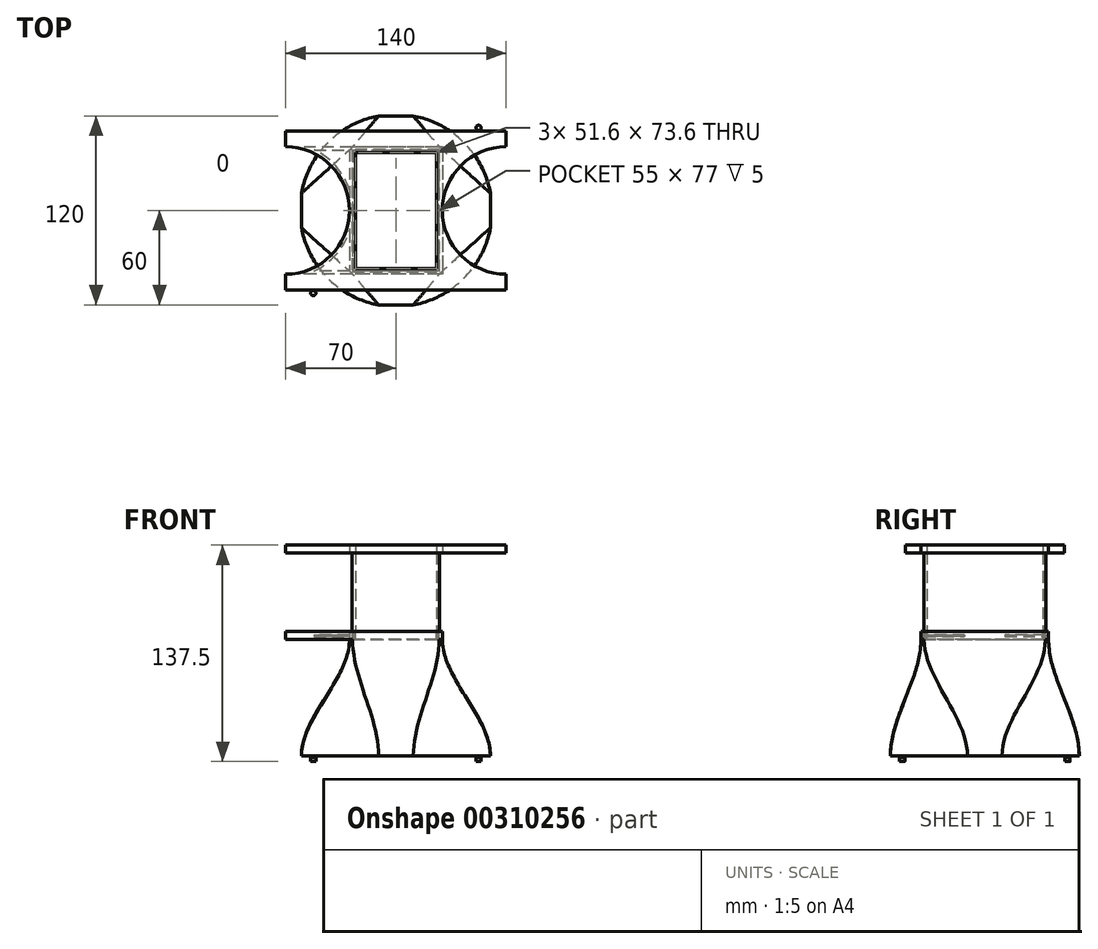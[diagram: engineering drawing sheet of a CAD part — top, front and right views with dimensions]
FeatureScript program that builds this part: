
annotation { "Feature Type Name" : "Feature", "Feature Type Description" : "" }
export const myFeature = defineFeature(function(context is Context, id is Id, definition is map)
    precondition{}
    {
        {
            var Q0;
            Q0=qCreatedBy(makeId("Top.planeOp"),FACE);
            var sketch = newSketch(context, id + "F0", { "sketchPlane" : qUnion([Q0])});
            skPoint(sketch, "E0.middle", {"position": v(0, 0) * mm});
            skLineSegment(sketch, "E1.bottom", {"start": v(-52.5, 52.5) * mm, "end": v(52.5, 52.5) * mm, "construction": true});
            skLineSegment(sketch, "E1.top", {"start": v(-52.5, -52.5) * mm, "end": v(52.5, -52.5) * mm, "construction": true});
            skLineSegment(sketch, "E1.left", {"start": v(-52.5, 52.5) * mm, "end": v(-52.5, -52.5) * mm, "construction": true});
            skLineSegment(sketch, "E1.right", {"start": v(52.5, 52.5) * mm, "end": v(52.5, -52.5) * mm, "construction": true});
            skLineSegment(sketch, "E2", {"start": v(0, 86.58) * mm, "end": v(0, -89.9) * mm, "construction": true});
            skLineSegment(sketch, "E3", {"start": v(-78.07, 0) * mm, "end": v(98.4, 0) * mm, "construction": true});
            skLineSegment(sketch, "E4.bottom", {"start": v(-60, -60) * mm, "end": v(60, -60) * mm});
            skLineSegment(sketch, "E4.top", {"start": v(-60, 60) * mm, "end": v(60, 60) * mm});
            skLineSegment(sketch, "E4.left", {"start": v(-60, -60) * mm, "end": v(-60, 60) * mm});
            skLineSegment(sketch, "E4.right", {"start": v(60, -60) * mm, "end": v(60, 60) * mm});
            skSolve(sketch);
        }
        {
            assignVariable(context, id + "F1", {"name" : "fan_flange_thickness", "anyValue" : 5 * mm});
        }
        {
            var Q0;
            Q0=makeQuery(id+"F0.imprint","IMPRINT",FACE,{"disambiguationData":[TD([[makeQuery(id+"F0.imprint","IMPRINT",EDGE,{"derivedFrom":sQuery(id+"F0.wireOp",EDGE,"E4.bottom")}),1.0]])]});
            extrude(context, id + "F2", {"entities" : qUnion([Q0]), "depth" : getVariable(context, 'fan_flange_thickness')});
        }
        {
            var Q0;
            Q0=makeQuery(id+"F2.opExtrude","CAP_FACE",FACE,{"disambiguationData":[OSD([sQuery(id+"F0.wireOp",EDGE,"E4.bottom"),sQuery(id+"F0.wireOp",EDGE,"E4.top"),sQuery(id+"F0.wireOp",EDGE,"E4.left"),sQuery(id+"F0.wireOp",EDGE,"E4.right")])],"isStart":false});
            var sketch = newSketch(context, id + "F3", { "sketchPlane" : qUnion([Q0])});
            skCircle(sketch, "E5", {"center": v(0, 0) * mm, "radius": 61 * mm});
            skSolve(sketch);
        }
        {
            var Q0;
            {var subQ0=sQuery(id+"F3.wireOp",EDGE,"E5");var subQ8=makeQuery(id+"F2.opExtrude","CAP_EDGE",EDGE,{"disambiguationData":[OSD([sQuery(id+"F0.wireOp",EDGE,"E4.top")])],"isStart":false});var subQ11=makeQuery(id+"F3.imprint","INTERSECT",VERTEX,{"disambiguationData":[OD(0.0)],"derivedFrom":[subQ8,subQ0]});Q0=makeQuery(id+"F3.imprint","IMPRINT",FACE,{"disambiguationData":[TD([[makeQuery(id+"F3.imprint","IMPRINT",EDGE,{"disambiguationData":[TD([[subQ11,1.0]])],"derivedFrom":subQ0}),1.0]])]});}
            extrude(context, id + "F4", {"entities" : qUnion([Q0]), "depth" : 1 * mm});
        }
        {
            assignVariable(context, id + "F5", {"name" : "overall_height", "anyValue" : 80 * mm});
        }
        {
            assignVariable(context, id + "F6", {"name" : "conduit_clearance", "anyValue" : 2 * mm});
        }
        {
            var Q0;
            Q0=qCreatedBy(makeId("Top.planeOp"),FACE);
            cPlane(context, id + "F7", {"entities" : qUnion([Q0]), "cplaneType" : CPlaneType.OFFSET, "offset" : getVariable(context, 'overall_height'), "width" : 150 * mm, "height" : 150 * mm});
        }
        {
            var Q0;
            Q0=qCreatedBy(id+"F7.planeOp",FACE);
            var sketch = newSketch(context, id + "F8", { "sketchPlane" : qUnion([Q0])});
            skLineSegment(sketch, "E6", {"start": v(-70, -38.5) * mm, "end": v(-70, 41.5) * mm, "construction": true});
            skArc(sketch, "E7", {"start": v(-70, -38.5) * mm, "mid": v(-31.5, 0) * mm, "end": v(-70, 38.5) * mm, "construction": true});
            skArc(sketch, "E8.0", {"start": v(-70, -40.5) * mm, "mid": v(-29.5, 0) * mm, "end": v(-70, 40.5) * mm});
            skLineSegment(sketch, "E9", {"start": v(-70, -40.5) * mm, "end": v(-70, -38.5) * mm, "construction": true});
            skLineSegment(sketch, "E10", {"start": v(-70, 41.5) * mm, "end": v(-70, 40.5) * mm, "construction": true});
            skLineSegment(sketch, "E11", {"start": v(-31.5, 45.47) * mm, "end": v(-31.5, -34.61) * mm, "construction": true});
            skLineSegment(sketch, "E12.MirrorCS", {"start": v(70, -40.5) * mm, "end": v(70, -38.5) * mm, "construction": true});
            skLineSegment(sketch, "E13.MirrorCS", {"start": v(70, 41.5) * mm, "end": v(70, 40.5) * mm, "construction": true});
            skLineSegment(sketch, "E14.MirrorCS", {"start": v(70, -38.5) * mm, "end": v(70, 41.5) * mm, "construction": true});
            skArc(sketch, "E15.MirrorCS", {"start": v(70, -40.5) * mm, "mid": v(29.5, 0) * mm, "end": v(70, 40.5) * mm});
            skArc(sketch, "E16.MirrorCS", {"start": v(70, -38.5) * mm, "mid": v(31.5, 0) * mm, "end": v(70, 38.5) * mm, "construction": true});
            skLineSegment(sketch, "E17.MirrorCS", {"start": v(31.5, 45.47) * mm, "end": v(31.5, -34.61) * mm, "construction": true});
            skLineSegment(sketch, "E18", {"start": v(-70, 40.5) * mm, "end": v(70, 40.5) * mm});
            skLineSegment(sketch, "E19", {"start": v(70, -40.5) * mm, "end": v(-70, -40.5) * mm});
            skLineSegment(sketch, "E20.bottom", {"start": v(-28.5, 38.5) * mm, "end": v(28.5, 38.5) * mm, "construction": true});
            skLineSegment(sketch, "E20.top", {"start": v(-28.5, -38.5) * mm, "end": v(28.5, -38.5) * mm, "construction": true});
            skLineSegment(sketch, "E20.left", {"start": v(-28.5, 38.5) * mm, "end": v(-28.5, -38.5) * mm, "construction": true});
            skLineSegment(sketch, "E20.right", {"start": v(28.5, 38.5) * mm, "end": v(28.5, -38.5) * mm, "construction": true});
            skPoint(sketch, "E20.middle", {"position": v(0, 0) * mm});
            skLineSegment(sketch, "E21", {"start": v(-29.5, 40.5) * mm, "end": v(-29.5, -40.5) * mm});
            skLineSegment(sketch, "E22.MirrorCS", {"start": v(29.5, 40.5) * mm, "end": v(29.5, -40.5) * mm});
            skLineSegment(sketch, "E23", {"start": v(-27.5, 40.5) * mm, "end": v(-29.5, 38.5) * mm});
            skLineSegment(sketch, "E24.MirrorCS", {"start": v(27.5, 40.5) * mm, "end": v(29.5, 38.5) * mm});
            skLineSegment(sketch, "E25.MirrorCS", {"start": v(27.5, -40.5) * mm, "end": v(29.5, -38.5) * mm});
            skLineSegment(sketch, "E26.MirrorCS", {"start": v(-27.5, -40.5) * mm, "end": v(-29.5, -38.5) * mm});
            skSolve(sketch);
        }
        {
            var Q0;
            {var subQ6=sQuery(id+"F8.wireOp",EDGE,"E24.MirrorCS");Q0=makeQuery(id+"F8.imprint","IMPRINT",FACE,{"disambiguationData":[TD([[makeQuery(id+"F8.imprint","IMPRINT",EDGE,{"derivedFrom":subQ6}),-1.0]])]});}
            extrude(context, id + "F9", {"entities" : qUnion([Q0]), "depth" : getVariable(context, 'fan_flange_thickness')});
        }
        {
            var Q0;
            {var subQ0=sQuery(id+"F8.wireOp",EDGE,"E22.MirrorCS");var subQ1=sQuery(id+"F8.wireOp",EDGE,"E18");var subQ2=sQuery(id+"F8.wireOp",EDGE,"E15.MirrorCS");var subQ3=sQuery(id+"F8.wireOp",EDGE,"E19");var subQ4=sQuery(id+"F8.wireOp",EDGE,"E21");var subQ5=sQuery(id+"F8.wireOp",EDGE,"E8.0");Q0=makeQuery(id+"F12.boolean.opBoolean","MERGE",FACE,{"derivedFrom":[makeQuery(id+"F9.opExtrude","CAP_FACE",FACE,{"disambiguationData":[OSD([subQ1,subQ3,subQ4,subQ0])],"isStart":false}),makeQuery(id+"F12.opExtrude","CAP_FACE",FACE,{"disambiguationData":[OSD([subQ5,subQ3,subQ4])],"isStart":false}),makeQuery(id+"F12.opExtrude","CAP_FACE",FACE,{"disambiguationData":[OSD([subQ5,subQ1,subQ4])],"isStart":false}),makeQuery(id+"F12.opExtrude","CAP_FACE",FACE,{"disambiguationData":[OSD([subQ2,subQ3,subQ0])],"isStart":false}),makeQuery(id+"F12.opExtrude","CAP_FACE",FACE,{"disambiguationData":[OSD([subQ2,subQ1,subQ0])],"isStart":false})]});}
            var sketch = newSketch(context, id + "F10", { "sketchPlane" : qUnion([Q0])});
            skLineSegment(sketch, "E27.0", {"start": v(27.5, -38.5) * mm, "end": v(27.5, 38.5) * mm});
            skLineSegment(sketch, "E27.1", {"start": v(-27.5, -38.5) * mm, "end": v(27.5, -38.5) * mm});
            skLineSegment(sketch, "E27.2", {"start": v(-27.5, 38.5) * mm, "end": v(-27.5, -38.5) * mm});
            skLineSegment(sketch, "E27.3", {"start": v(27.5, 38.5) * mm, "end": v(-27.5, 38.5) * mm});
            skSolve(sketch);
        }
        {
            var Q0;
            Q0=makeQuery(id+"F4.opExtrude","CAP_FACE",FACE,{"disambiguationData":[OSD([sQuery(id+"F0.wireOp",EDGE,"E4.bottom"),sQuery(id+"F0.wireOp",EDGE,"E4.top"),sQuery(id+"F0.wireOp",EDGE,"E4.left"),sQuery(id+"F0.wireOp",EDGE,"E4.right"),sQuery(id+"F3.wireOp",EDGE,"E5")])],"isStart":false});
            var Q1;
            Q1=makeQuery(id+"F9.opExtrude","CAP_FACE",FACE,{"disambiguationData":[OSD([sQuery(id+"F8.wireOp",EDGE,"E18"),sQuery(id+"F8.wireOp",EDGE,"E19"),sQuery(id+"F8.wireOp",EDGE,"E21"),sQuery(id+"F8.wireOp",EDGE,"E22.MirrorCS")])],"isStart":true});
            loft(context, id + "F11", {"startCondition" : LoftEndDerivativeType.MATCH_TANGENT, "startMagnitude" : 1, "endCondition" : LoftEndDerivativeType.MATCH_TANGENT, "endMagnitude" : 1, "sheetProfilesArray" : [{ "sheetProfileEntities" : qUnion([Q0]) }, { "sheetProfileEntities" : qUnion([Q1]) }]});
        }
        {
            var Q0;
            {var subQ0=sQuery(id+"F8.wireOp",EDGE,"E18");var subQ1=sQuery(id+"F8.wireOp",EDGE,"E15.MirrorCS");var subQ2=makeQuery(id+"F8.imprint","INTERSECT",VERTEX,{"derivedFrom":[subQ1,subQ0]});Q0=makeQuery(id+"F8.imprint","IMPRINT",FACE,{"disambiguationData":[TD([[makeQuery(id+"F8.imprint","IMPRINT",EDGE,{"disambiguationData":[TD([[subQ2,1.0]])],"derivedFrom":subQ1}),1.0]])]});}
            var Q1;
            {var subQ0=sQuery(id+"F8.wireOp",EDGE,"E19");var subQ1=sQuery(id+"F8.wireOp",EDGE,"E15.MirrorCS");var subQ2=makeQuery(id+"F8.imprint","INTERSECT",VERTEX,{"derivedFrom":[subQ1,subQ0]});Q1=makeQuery(id+"F8.imprint","IMPRINT",FACE,{"disambiguationData":[TD([[makeQuery(id+"F8.imprint","IMPRINT",EDGE,{"disambiguationData":[TD([[subQ2,-1.0]])],"derivedFrom":subQ1}),1.0]])]});}
            var Q2;
            {var subQ0=sQuery(id+"F8.wireOp",EDGE,"E19");var subQ1=sQuery(id+"F8.wireOp",EDGE,"E8.0");var subQ2=makeQuery(id+"F8.imprint","INTERSECT",VERTEX,{"derivedFrom":[subQ1,subQ0]});Q2=makeQuery(id+"F8.imprint","IMPRINT",FACE,{"disambiguationData":[TD([[makeQuery(id+"F8.imprint","IMPRINT",EDGE,{"disambiguationData":[TD([[subQ2,-1.0]])],"derivedFrom":subQ1}),-1.0]])]});}
            var Q3;
            {var subQ0=sQuery(id+"F8.wireOp",EDGE,"E18");var subQ1=sQuery(id+"F8.wireOp",EDGE,"E8.0");var subQ2=makeQuery(id+"F8.imprint","INTERSECT",VERTEX,{"derivedFrom":[subQ1,subQ0]});Q3=makeQuery(id+"F8.imprint","IMPRINT",FACE,{"disambiguationData":[TD([[makeQuery(id+"F8.imprint","IMPRINT",EDGE,{"disambiguationData":[TD([[subQ2,1.0]])],"derivedFrom":subQ1}),-1.0]])]});}
            var Q4;
            {var subQ3=sQuery(id+"F8.wireOp",EDGE,"E23");Q4=makeQuery(id+"F8.imprint","IMPRINT",FACE,{"disambiguationData":[TD([[makeQuery(id+"F8.imprint","IMPRINT",EDGE,{"derivedFrom":subQ3}),-1.0]])]});}
            var Q5;
            {var subQ3=sQuery(id+"F8.wireOp",EDGE,"E24.MirrorCS");Q5=makeQuery(id+"F8.imprint","IMPRINT",FACE,{"disambiguationData":[TD([[makeQuery(id+"F8.imprint","IMPRINT",EDGE,{"derivedFrom":subQ3}),1.0]])]});}
            var Q6;
            {var subQ3=sQuery(id+"F8.wireOp",EDGE,"E25.MirrorCS");Q6=makeQuery(id+"F8.imprint","IMPRINT",FACE,{"disambiguationData":[TD([[makeQuery(id+"F8.imprint","IMPRINT",EDGE,{"derivedFrom":subQ3}),-1.0]])]});}
            var Q7;
            {var subQ3=sQuery(id+"F8.wireOp",EDGE,"E26.MirrorCS");Q7=makeQuery(id+"F8.imprint","IMPRINT",FACE,{"disambiguationData":[TD([[makeQuery(id+"F8.imprint","IMPRINT",EDGE,{"derivedFrom":subQ3}),1.0]])]});}
            extrude(context, id + "F12", {"entities" : qUnion([Q0, Q1, Q2, Q3, Q4, Q5, Q6, Q7]), "operationType" : NewBodyOperationType.ADD, "depth" : getVariable(context, 'fan_flange_thickness')});
        }
        {
            var Q0;
            Q0=makeQuery(id+"F10.imprint","IMPRINT",FACE,{"disambiguationData":[TD([[makeQuery(id+"F10.imprint","IMPRINT",EDGE,{"derivedFrom":sQuery(id+"F10.wireOp",EDGE,"E27.0")}),1.0]])]});
            extrude(context, id + "F13", {"entities" : qUnion([Q0]), "operationType" : NewBodyOperationType.REMOVE, "oppositeDirection" : true, "depth" : getVariable(context, 'fan_flange_thickness')});
        }
        {
            var Q0;
            Q0=makeQuery(id+"F2.opExtrude","CAP_FACE",FACE,{"disambiguationData":[OSD([sQuery(id+"F0.wireOp",EDGE,"E4.bottom"),sQuery(id+"F0.wireOp",EDGE,"E4.top"),sQuery(id+"F0.wireOp",EDGE,"E4.left"),sQuery(id+"F0.wireOp",EDGE,"E4.right")])],"isStart":true});
            var sketch = newSketch(context, id + "F14", { "sketchPlane" : qUnion([Q0])});
            skCircle(sketch, "E28", {"center": v(0, 0) * mm, "radius": 59.5 * mm});
            skCircle(sketch, "E29", {"center": v(-52.5, -52.5) * mm, "radius": 1.65 * mm});
            skCircle(sketch, "E30.MirrorC", {"center": v(52.5, -52.5) * mm, "radius": 1.65 * mm});
            skCircle(sketch, "E31.MirrorC", {"center": v(52.5, 52.5) * mm, "radius": 1.65 * mm});
            skCircle(sketch, "E32.MirrorC", {"center": v(-52.5, 52.5) * mm, "radius": 1.65 * mm});
            skSolve(sketch);
        }
        {
            var Q0;
            Q0=makeQuery(id+"F14.imprint","IMPRINT",FACE,{"disambiguationData":[TD([[makeQuery(id+"F14.imprint","IMPRINT",EDGE,{"derivedFrom":sQuery(id+"F14.wireOp",EDGE,"E28")}),1.0]])]});
            var Q1;
            Q1=makeQuery(id+"F14.imprint","IMPRINT",FACE,{"disambiguationData":[TD([[makeQuery(id+"F14.imprint","IMPRINT",EDGE,{"derivedFrom":sQuery(id+"F14.wireOp",EDGE,"E29")}),1.0]])]});
            var Q2;
            Q2=makeQuery(id+"F14.imprint","IMPRINT",FACE,{"disambiguationData":[TD([[makeQuery(id+"F14.imprint","IMPRINT",EDGE,{"derivedFrom":sQuery(id+"F14.wireOp",EDGE,"E32.MirrorC")}),-1.0]])]});
            var Q3;
            Q3=makeQuery(id+"F14.imprint","IMPRINT",FACE,{"disambiguationData":[TD([[makeQuery(id+"F14.imprint","IMPRINT",EDGE,{"derivedFrom":sQuery(id+"F14.wireOp",EDGE,"E30.MirrorC")}),-1.0]])]});
            var Q4;
            Q4=makeQuery(id+"F14.imprint","IMPRINT",FACE,{"disambiguationData":[TD([[makeQuery(id+"F14.imprint","IMPRINT",EDGE,{"derivedFrom":sQuery(id+"F14.wireOp",EDGE,"E31.MirrorC")}),1.0]])]});
            extrude(context, id + "F15", {"entities" : qUnion([Q0, Q1, Q2, Q3, Q4]), "operationType" : NewBodyOperationType.REMOVE, "oppositeDirection" : true, "depth" : getVariable(context, 'fan_flange_thickness') + 1 * mm});
        }
        {
            var Q0;
            Q0=makeQuery(id+"F0.imprint","IMPRINT",FACE,{"disambiguationData":[TD([[makeQuery(id+"F0.imprint","IMPRINT",EDGE,{"derivedFrom":sQuery(id+"F0.wireOp",EDGE,"E4.bottom")}),1.0]])]});
            var sketch = newSketch(context, id + "F16", { "sketchPlane" : qUnion([Q0])});
            skCircle(sketch, "E33.cCircle", {"center": v(-52.5, -52.5) * mm, "radius": 3.25 * mm, "construction": true});
            skLineSegment(sketch, "E33.0", {"start": v(-53.62, -55.55) * mm, "end": v(-55.7, -53.06) * mm});
            skLineSegment(sketch, "E33.1", {"start": v(-55.7, -53.06) * mm, "end": v(-54.58, -50) * mm});
            skLineSegment(sketch, "E33.2", {"start": v(-54.58, -50) * mm, "end": v(-51.38, -49.45) * mm});
            skLineSegment(sketch, "E33.3", {"start": v(-51.38, -49.45) * mm, "end": v(-49.3, -51.94) * mm});
            skLineSegment(sketch, "E33.4", {"start": v(-49.3, -51.94) * mm, "end": v(-50.42, -55) * mm});
            skLineSegment(sketch, "E33.5", {"start": v(-50.42, -55) * mm, "end": v(-53.62, -55.55) * mm});
            skLineSegment(sketch, "E34.MirrorCS", {"start": v(54.58, -50) * mm, "end": v(51.38, -49.45) * mm});
            skLineSegment(sketch, "E35.MirrorCS", {"start": v(53.62, -55.55) * mm, "end": v(55.7, -53.06) * mm});
            skCircle(sketch, "E36.MirrorC", {"center": v(52.5, -52.5) * mm, "radius": 3.25 * mm, "construction": true});
            skLineSegment(sketch, "E37.MirrorCS", {"start": v(55.7, -53.06) * mm, "end": v(54.58, -50) * mm});
            skLineSegment(sketch, "E38.MirrorCS", {"start": v(49.3, -51.94) * mm, "end": v(50.42, -55) * mm});
            skLineSegment(sketch, "E39.MirrorCS", {"start": v(51.38, -49.45) * mm, "end": v(49.3, -51.94) * mm});
            skLineSegment(sketch, "E40.MirrorCS", {"start": v(50.42, -55) * mm, "end": v(53.62, -55.55) * mm});
            skLineSegment(sketch, "E41.MirrorCS", {"start": v(51.38, 49.45) * mm, "end": v(49.3, 51.94) * mm});
            skLineSegment(sketch, "E42.MirrorCS", {"start": v(-53.62, 55.55) * mm, "end": v(-55.7, 53.06) * mm});
            skLineSegment(sketch, "E43.MirrorCS", {"start": v(55.7, 53.06) * mm, "end": v(54.58, 50) * mm});
            skLineSegment(sketch, "E44.MirrorCS", {"start": v(-51.38, 49.45) * mm, "end": v(-49.3, 51.94) * mm});
            skLineSegment(sketch, "E45.MirrorCS", {"start": v(49.3, 51.94) * mm, "end": v(50.42, 55) * mm});
            skLineSegment(sketch, "E46.MirrorCS", {"start": v(-55.7, 53.06) * mm, "end": v(-54.58, 50) * mm});
            skLineSegment(sketch, "E47.MirrorCS", {"start": v(-50.42, 55) * mm, "end": v(-53.62, 55.55) * mm});
            skLineSegment(sketch, "E48.MirrorCS", {"start": v(-49.3, 51.94) * mm, "end": v(-50.42, 55) * mm});
            skLineSegment(sketch, "E49.MirrorCS", {"start": v(-54.58, 50) * mm, "end": v(-51.38, 49.45) * mm});
            skLineSegment(sketch, "E50.MirrorCS", {"start": v(53.62, 55.55) * mm, "end": v(55.7, 53.06) * mm});
            skLineSegment(sketch, "E51.MirrorCS", {"start": v(54.58, 50) * mm, "end": v(51.38, 49.45) * mm});
            skLineSegment(sketch, "E52.MirrorCS", {"start": v(50.42, 55) * mm, "end": v(53.62, 55.55) * mm});
            skCircle(sketch, "E53.MirrorC", {"center": v(52.5, 52.5) * mm, "radius": 3.25 * mm, "construction": true});
            skCircle(sketch, "E54.MirrorC", {"center": v(-52.5, 52.5) * mm, "radius": 3.25 * mm, "construction": true});
            skSolve(sketch);
        }
        {
            var Q0;
            Q0 = qSketchRegion(id + "F16", true);
            extrude(context, id + "F17", {"entities" : qUnion([Q0]), "operationType" : NewBodyOperationType.REMOVE, "depth" : 2.5 * mm});
        }
        {
            var Q0;
            Q0=makeQuery(id+"F11.opLoft","CAP_FACE",FACE,{"disambiguationData":[OSD([sQuery(id+"F0.wireOp",EDGE,"E4.bottom"),sQuery(id+"F0.wireOp",EDGE,"E4.top"),sQuery(id+"F0.wireOp",EDGE,"E4.left"),sQuery(id+"F0.wireOp",EDGE,"E4.right"),sQuery(id+"F3.wireOp",EDGE,"E5")])],"isStart":true});
            var Q1;
            Q1=makeQuery(id+"F11.opLoft","CAP_FACE",FACE,{"disambiguationData":[OSD([sQuery(id+"F8.wireOp",EDGE,"E18"),sQuery(id+"F8.wireOp",EDGE,"E19"),sQuery(id+"F8.wireOp",EDGE,"E21"),sQuery(id+"F8.wireOp",EDGE,"E22.MirrorCS")])],"isStart":true});
            shell(context, id + "F18", {"entities" : qUnion([Q0, Q1]), "thickness" : getVariable(context, 'conduit_clearance')});
        }
        {
            var Q0;
            {var subQ0=sQuery(id+"F8.wireOp",EDGE,"E24.MirrorCS");var subQ1=sQuery(id+"F8.wireOp",EDGE,"E22.MirrorCS");var subQ2=sQuery(id+"F8.wireOp",EDGE,"E18");var subQ3=sQuery(id+"F8.wireOp",EDGE,"E15.MirrorCS");var subQ4=sQuery(id+"F8.wireOp",EDGE,"E25.MirrorCS");var subQ5=sQuery(id+"F8.wireOp",EDGE,"E19");var subQ6=sQuery(id+"F8.wireOp",EDGE,"E23");var subQ7=sQuery(id+"F8.wireOp",EDGE,"E21");var subQ8=sQuery(id+"F8.wireOp",EDGE,"E8.0");var subQ9=sQuery(id+"F8.wireOp",EDGE,"E26.MirrorCS");Q0=makeQuery(id+"F12.boolean.opBoolean","MERGE",FACE,{"derivedFrom":[makeQuery(id+"F9.opExtrude","CAP_FACE",FACE,{"disambiguationData":[OSD([subQ2,subQ5,subQ7,subQ1,subQ0,subQ6,subQ4,subQ9])],"isStart":false}),makeQuery(id+"F12.opExtrude","CAP_FACE",FACE,{"disambiguationData":[OSD([subQ8,subQ5,subQ7,subQ9])],"isStart":false}),makeQuery(id+"F12.opExtrude","CAP_FACE",FACE,{"disambiguationData":[OSD([subQ8,subQ2,subQ7,subQ6])],"isStart":false}),makeQuery(id+"F12.opExtrude","CAP_FACE",FACE,{"disambiguationData":[OSD([subQ3,subQ5,subQ1,subQ4])],"isStart":false}),makeQuery(id+"F12.opExtrude","CAP_FACE",FACE,{"disambiguationData":[OSD([subQ3,subQ2,subQ1,subQ0])],"isStart":false})]});}
            cPlane(context, id + "F19", {"entities" : qUnion([Q0]), "cplaneType" : CPlaneType.OFFSET, "offset" : 0 * mm, "width" : 150 * mm, "height" : 150 * mm});
        }
        {
            var Q0;
            Q0=qCreatedBy(id+"F19.planeOp",FACE);
            var sketch = newSketch(context, id + "F20", { "sketchPlane" : qUnion([Q0])});
            skLineSegment(sketch, "E55.0", {"start": v(-27, -38) * mm, "end": v(27, -38) * mm});
            skLineSegment(sketch, "E55.1", {"start": v(-27, 38) * mm, "end": v(-27, -38) * mm});
            skLineSegment(sketch, "E55.2", {"start": v(27, 38) * mm, "end": v(-27, 38) * mm});
            skLineSegment(sketch, "E55.3", {"start": v(27, -38) * mm, "end": v(27, 38) * mm});
            skLineSegment(sketch, "E56.0", {"start": v(-25.8, 36.8) * mm, "end": v(-25.8, -36.8) * mm});
            skLineSegment(sketch, "E56.1", {"start": v(25.8, 36.8) * mm, "end": v(-25.8, 36.8) * mm});
            skLineSegment(sketch, "E56.2", {"start": v(25.8, -36.8) * mm, "end": v(25.8, 36.8) * mm});
            skLineSegment(sketch, "E56.3", {"start": v(-25.8, -36.8) * mm, "end": v(25.8, -36.8) * mm});
            skSolve(sketch);
        }
        {
            var Q0;
            Q0=makeQuery(id+"F20.imprint","IMPRINT",FACE,{"disambiguationData":[TD([[makeQuery(id+"F20.imprint","IMPRINT",EDGE,{"derivedFrom":sQuery(id+"F20.wireOp",EDGE,"E55.0")}),1.0]])]});
            extrude(context, id + "F21", {"entities" : qUnion([Q0]), "oppositeDirection" : true, "depth" : 5 * mm});
        }
        {
            var Q0;
            Q0=qCreatedBy(id+"F19.planeOp",FACE);
            cPlane(context, id + "F22", {"entities" : qUnion([Q0]), "cplaneType" : CPlaneType.OFFSET, "offset" : 50 * mm, "width" : 150 * mm, "height" : 150 * mm});
        }
        {
            var Q0;
            Q0=qCreatedBy(id+"F22.planeOp",FACE);
            var sketch = newSketch(context, id + "F23", { "sketchPlane" : qUnion([Q0])});
            skArc(sketch, "E57.1", {"start": v(-70, -40.5) * mm, "mid": v(-29.5, 0) * mm, "end": v(-70, 40.5) * mm});
            skArc(sketch, "E57.3", {"start": v(70, -40.5) * mm, "mid": v(29.5, 0) * mm, "end": v(70, 40.5) * mm});
            skLineSegment(sketch, "E58.0", {"start": v(-25.8, 36.8) * mm, "end": v(-25.8, -36.8) * mm});
            skLineSegment(sketch, "E58.1", {"start": v(25.8, 36.8) * mm, "end": v(-25.8, 36.8) * mm});
            skLineSegment(sketch, "E58.2", {"start": v(25.8, -36.8) * mm, "end": v(25.8, 36.8) * mm});
            skLineSegment(sketch, "E58.3", {"start": v(-25.8, -36.8) * mm, "end": v(25.8, -36.8) * mm});
            skLineSegment(sketch, "E59.top", {"start": v(-70, 50.5) * mm, "end": v(70, 50.5) * mm});
            skLineSegment(sketch, "E59.left", {"start": v(-70, 40.5) * mm, "end": v(-70, 50.5) * mm});
            skLineSegment(sketch, "E59.right", {"start": v(70, 40.5) * mm, "end": v(70, 50.5) * mm});
            skLineSegment(sketch, "E60.MirrorCS", {"start": v(70, -40.5) * mm, "end": v(70, -50.5) * mm});
            skLineSegment(sketch, "E61.MirrorCS", {"start": v(-70, -40.5) * mm, "end": v(-70, -50.5) * mm});
            skLineSegment(sketch, "E62.MirrorCS", {"start": v(-70, -50.5) * mm, "end": v(70, -50.5) * mm});
            skSolve(sketch);
        }
        {
            var Q0;
            Q0=makeQuery(id+"F23.imprint","IMPRINT",FACE,{"disambiguationData":[TD([[makeQuery(id+"F23.imprint","IMPRINT",EDGE,{"derivedFrom":sQuery(id+"F23.wireOp",EDGE,"E57.1")}),-1.0]])]});
            extrude(context, id + "F24", {"entities" : qUnion([Q0]), "depth" : getVariable(context, 'fan_flange_thickness')});
        }
        {
            var Q0;
            Q0=qCreatedBy(id+"F19.planeOp",FACE);
            var sketch = newSketch(context, id + "F25", { "sketchPlane" : qUnion([Q0])});
            skLineSegment(sketch, "E63.0", {"start": v(25.8, 36.8) * mm, "end": v(-25.8, 36.8) * mm});
            skLineSegment(sketch, "E63.1", {"start": v(25.8, -36.8) * mm, "end": v(25.8, 36.8) * mm});
            skLineSegment(sketch, "E63.2", {"start": v(-25.8, -36.8) * mm, "end": v(25.8, -36.8) * mm});
            skLineSegment(sketch, "E63.3", {"start": v(-25.8, 36.8) * mm, "end": v(-25.8, -36.8) * mm});
            skLineSegment(sketch, "E64.0", {"start": v(27.8, 38.8) * mm, "end": v(-27.8, 38.8) * mm});
            skLineSegment(sketch, "E64.1", {"start": v(27.8, -38.8) * mm, "end": v(27.8, 38.8) * mm});
            skLineSegment(sketch, "E64.2", {"start": v(-27.8, -38.8) * mm, "end": v(27.8, -38.8) * mm});
            skLineSegment(sketch, "E64.3", {"start": v(-27.8, 38.8) * mm, "end": v(-27.8, -38.8) * mm});
            skSolve(sketch);
        }
        {
            var Q0;
            Q0 = qSketchRegion(id + "F25", true);
            var Q1;
            Q1=makeQuery(id+"F24.opExtrude","CAP_FACE",FACE,{"disambiguationData":[OSD([sQuery(id+"F23.wireOp",EDGE,"E57.1"),sQuery(id+"F23.wireOp",EDGE,"E57.3"),sQuery(id+"F23.wireOp",EDGE,"E58.0"),sQuery(id+"F23.wireOp",EDGE,"E58.1"),sQuery(id+"F23.wireOp",EDGE,"E58.2"),sQuery(id+"F23.wireOp",EDGE,"E58.3"),sQuery(id+"F23.wireOp",EDGE,"E59.top"),sQuery(id+"F23.wireOp",EDGE,"E59.left"),sQuery(id+"F23.wireOp",EDGE,"E59.right"),sQuery(id+"F23.wireOp",EDGE,"E60.MirrorCS"),sQuery(id+"F23.wireOp",EDGE,"E61.MirrorCS"),sQuery(id+"F23.wireOp",EDGE,"E62.MirrorCS")])],"isStart":true});
            var Q2;
            Q2=makeQuery(id+"F24.opExtrude","CAP_FACE",FACE,{"disambiguationData":[OSD([sQuery(id+"F23.wireOp",EDGE,"E57.1"),sQuery(id+"F23.wireOp",EDGE,"E57.3"),sQuery(id+"F23.wireOp",EDGE,"E58.0"),sQuery(id+"F23.wireOp",EDGE,"E58.1"),sQuery(id+"F23.wireOp",EDGE,"E58.2"),sQuery(id+"F23.wireOp",EDGE,"E58.3"),sQuery(id+"F23.wireOp",EDGE,"E59.top"),sQuery(id+"F23.wireOp",EDGE,"E59.left"),sQuery(id+"F23.wireOp",EDGE,"E59.right"),sQuery(id+"F23.wireOp",EDGE,"E60.MirrorCS"),sQuery(id+"F23.wireOp",EDGE,"E61.MirrorCS"),sQuery(id+"F23.wireOp",EDGE,"E62.MirrorCS")])],"isStart":true});
            extrude(context, id + "F26", {"entities" : qUnion([Q0, Q1]), "endBound" : BoundingType.UP_TO_NEXT, "endBoundEntityFace" : qUnion([Q2]), "depth" : 25 * mm});
        }
        {
            var Q0;
            Q0=makeQuery(id+"F26.opExtrude","SWEPT_BODY",BODY,{"disambiguationData":[OSD([sQuery(id+"F23.wireOp",EDGE,"E57.1"),sQuery(id+"F23.wireOp",EDGE,"E57.3"),sQuery(id+"F23.wireOp",EDGE,"E58.0"),sQuery(id+"F23.wireOp",EDGE,"E58.1"),sQuery(id+"F23.wireOp",EDGE,"E58.2"),sQuery(id+"F23.wireOp",EDGE,"E58.3"),sQuery(id+"F23.wireOp",EDGE,"E59.top"),sQuery(id+"F23.wireOp",EDGE,"E59.left"),sQuery(id+"F23.wireOp",EDGE,"E59.right"),sQuery(id+"F23.wireOp",EDGE,"E60.MirrorCS"),sQuery(id+"F23.wireOp",EDGE,"E61.MirrorCS"),sQuery(id+"F23.wireOp",EDGE,"E62.MirrorCS")])]});
            deleteBodies(context, id + "F27", {"entities" : qUnion([Q0])});
        }
    });
